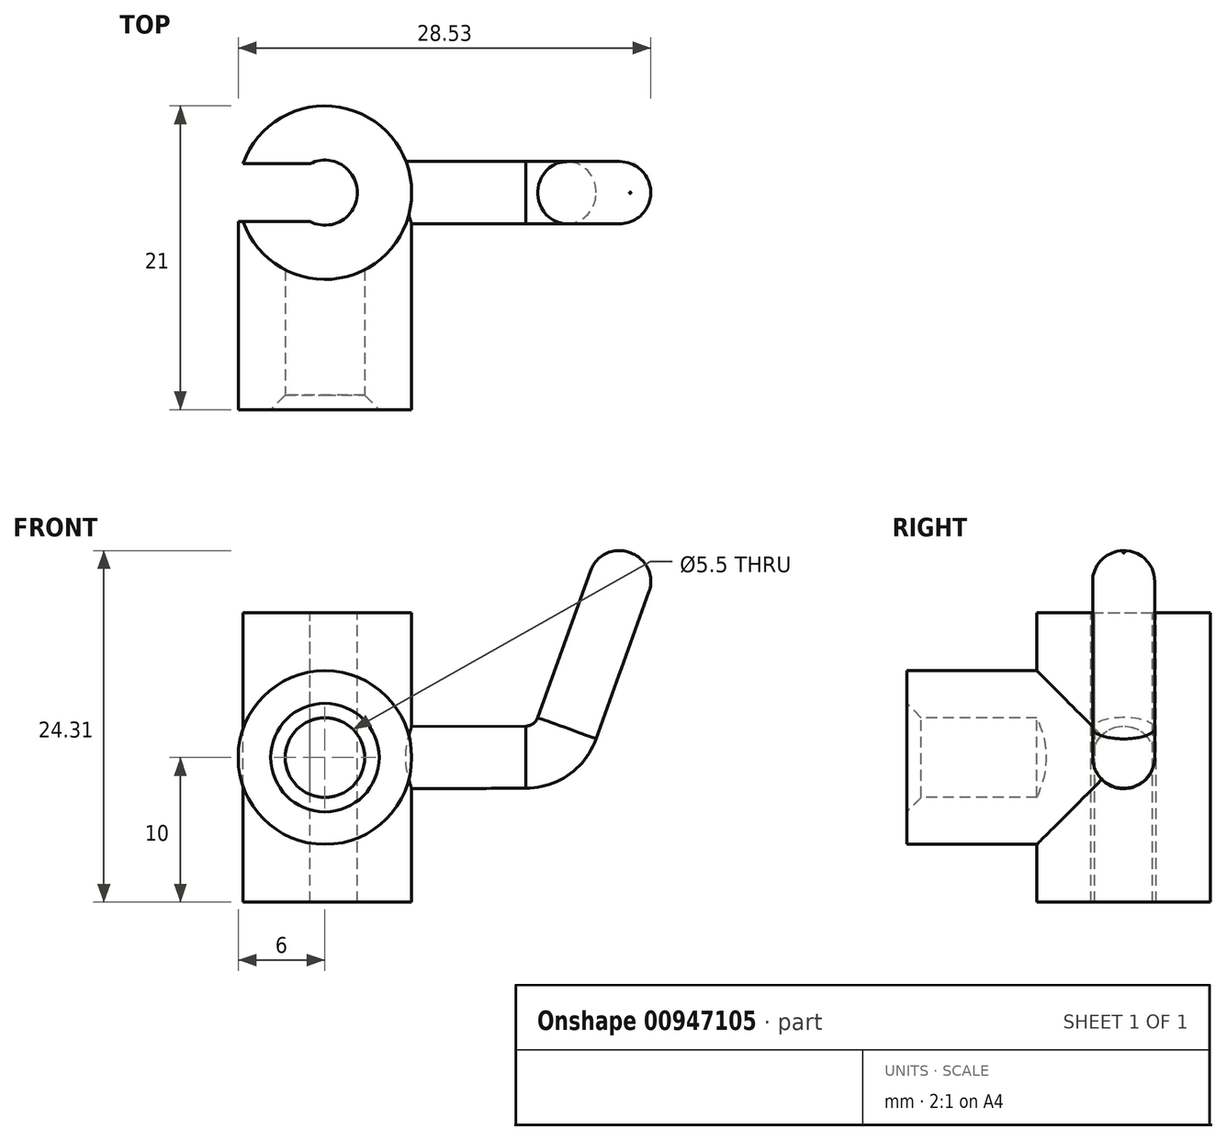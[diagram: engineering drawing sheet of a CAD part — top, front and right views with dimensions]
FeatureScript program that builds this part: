
annotation { "Feature Type Name" : "Feature", "Feature Type Description" : "" }
export const myFeature = defineFeature(function(context is Context, id is Id, definition is map)
    precondition{}
    {
        {
            var Q0;
            Q0=qCreatedBy(makeId("Top.planeOp"),FACE);
            var sketch = newSketch(context, id + "F0", { "sketchPlane" : qUnion([Q0])});
            skCircle(sketch, "E0", {"center": v(0, 0) * mm, "radius": 6 * mm});
            skSolve(sketch);
        }
        {
            var Q0;
            Q0=makeQuery(id+"F0.imprint","IMPRINT",FACE,{"disambiguationData":[TD([[makeQuery(id+"F0.imprint","IMPRINT",EDGE,{"derivedFrom":sQuery(id+"F0.wireOp",EDGE,"E0")}),1.0]])]});
            extrude(context, id + "F1", {"entities" : qUnion([Q0]), "oppositeDirection" : true, "depth" : 20 * mm, "offsetDistance" : 25 * mm});
        }
        {
            var Q0;
            Q0=makeQuery(id+"F1.opExtrude","CAP_FACE",FACE,{"disambiguationData":[OSD([sQuery(id+"F0.wireOp",EDGE,"E0")])],"isStart":true});
            var sketch = newSketch(context, id + "F2", { "sketchPlane" : qUnion([Q0])});
            skCircle(sketch, "E1", {"center": v(0, 0) * mm, "radius": 2.25 * mm});
            skSolve(sketch);
        }
        {
            var Q0;
            Q0=qCreatedBy(makeId("Front.planeOp"),FACE);
            cPlane(context, id + "F3", {"entities" : qUnion([Q0]), "cplaneType" : CPlaneType.OFFSET, "offset" : 15 * mm, "width" : 150 * mm, "height" : 150 * mm});
        }
        {
            var Q0;
            Q0=qCreatedBy(id+"F3.planeOp",FACE);
            var sketch = newSketch(context, id + "F4", { "sketchPlane" : qUnion([Q0])});
            skCircle(sketch, "E2", {"center": v(0, -10) * mm, "radius": 6 * mm});
            skCircle(sketch, "E3", {"center": v(0, -10) * mm, "radius": 2.75 * mm});
            skSolve(sketch);
        }
        {
            var Q0;
            Q0=makeQuery(id+"F4.imprint","IMPRINT",FACE,{"disambiguationData":[TD([[makeQuery(id+"F4.imprint","IMPRINT",EDGE,{"derivedFrom":sQuery(id+"F4.wireOp",EDGE,"E2")}),1.0]])]});
            extrude(context, id + "F5", {"entities" : qUnion([Q0]), "operationType" : NewBodyOperationType.ADD, "oppositeDirection" : true, "depth" : 15 * mm, "offsetDistance" : 25 * mm});
        }
        {
            var Q0;
            Q0=makeQuery(id+"F1.opExtrude","CAP_FACE",FACE,{"disambiguationData":[OSD([sQuery(id+"F0.wireOp",EDGE,"E0")])],"isStart":true});
            var sketch = newSketch(context, id + "F6", { "sketchPlane" : qUnion([Q0])});
            skLineSegment(sketch, "E4.bottom", {"start": v(-8.53, 2) * mm, "end": v(0, 2) * mm});
            skLineSegment(sketch, "E4.top", {"start": v(-8.53, -2) * mm, "end": v(0, -2) * mm});
            skLineSegment(sketch, "E4.left", {"start": v(-8.53, 2) * mm, "end": v(-8.53, -2) * mm});
            skPoint(sketch, "E4.middle", {"position": v(0, 0) * mm});
            skLineSegment(sketch, "E5", {"start": v(0, 2) * mm, "end": v(0, -2) * mm});
            skSolve(sketch);
        }
        {
            var Q0;
            {var subQ0=sQuery(id+"F6.wireOp",EDGE,"E4.bottom");var subQ1=makeQuery(id+"F1.opExtrude","CAP_EDGE",EDGE,{"disambiguationData":[OSD([sQuery(id+"F0.wireOp",EDGE,"E0")])],"isStart":true});var subQ2=makeQuery(id+"F6.imprint","INTERSECT",VERTEX,{"derivedFrom":[subQ1,subQ0]});Q0=makeQuery(id+"F6.imprint","IMPRINT",FACE,{"disambiguationData":[TD([[makeQuery(id+"F6.imprint","IMPRINT",EDGE,{"disambiguationData":[TD([[subQ2,-1.0]])],"derivedFrom":subQ0}),-1.0]])]});}
            var Q1;
            {var subQ0=sQuery(id+"F6.wireOp",EDGE,"E5");Q1=makeQuery(id+"F6.imprint","IMPRINT",FACE,{"disambiguationData":[TD([[makeQuery(id+"F6.imprint","IMPRINT",EDGE,{"derivedFrom":subQ0}),-1.0]])]});}
            var Q2;
            {var subQ0=sQuery(id+"F6.wireOp",EDGE,"E4.left");Q2=makeQuery(id+"F6.imprint","IMPRINT",FACE,{"disambiguationData":[TD([[makeQuery(id+"F6.imprint","IMPRINT",EDGE,{"derivedFrom":subQ0}),1.0]])]});}
            extrude(context, id + "F7", {"entities" : qUnion([Q0, Q1, Q2]), "operationType" : NewBodyOperationType.REMOVE, "endBound" : BoundingType.UP_TO_NEXT, "oppositeDirection" : true, "depth" : 25 * mm, "offsetDistance" : 25 * mm});
        }
        {
            var Q0;
            Q0=makeQuery(id+"F5.opExtrude","CAP_EDGE",EDGE,{"disambiguationData":[OSD([sQuery(id+"F4.wireOp",EDGE,"E3")])],"isStart":true});
            chamfer(context, id + "F8", {"entities" : qUnion([Q0]), "width" : 1 * mm, "tangentPropagation" : true});
        }
        {
            var Q0;
            Q0=qCreatedBy(makeId("Right.planeOp"),FACE);
            cPlane(context, id + "F9", {"entities" : qUnion([Q0]), "cplaneType" : CPlaneType.OFFSET, "offset" : 6 * mm, "width" : 150 * mm, "height" : 150 * mm});
        }
        {
            var Q0;
            Q0=qCreatedBy(makeId("Front.planeOp"),FACE);
            var sketch = newSketch(context, id + "F10", { "sketchPlane" : qUnion([Q0])});
            skLineSegment(sketch, "E6", {"start": v(0, -10) * mm, "end": v(13.9, -9.95) * mm});
            skLineSegment(sketch, "E7", {"start": v(16.71, -7.96) * mm, "end": v(21.08, 4.17) * mm});
            skPoint(sketch, "E8.visualSharp", {"position": v(16, -9.94) * mm});
            skArc(sketch, "E8.filletArc", {"start": v(13.9, -9.95) * mm, "mid": v(15.62, -9.4) * mm, "end": v(16.71, -7.96) * mm});
            skSolve(sketch);
        }
        {
            var Q0;
            Q0=qCreatedBy(id+"F9.planeOp",FACE);
            var sketch = newSketch(context, id + "F11", { "sketchPlane" : qUnion([Q0])});
            skCircle(sketch, "E9", {"center": v(0, -10) * mm, "radius": 2.15 * mm});
            skSolve(sketch);
        }
        {
            var Q0;
            Q0=makeQuery(id+"F11.imprint","IMPRINT",FACE,{"disambiguationData":[TD([[makeQuery(id+"F11.imprint","IMPRINT",EDGE,{"derivedFrom":sQuery(id+"F11.wireOp",EDGE,"E9")}),1.0]])]});
            var Q1;
            Q1=sQuery(id+"F10.wireOp",EDGE,"E6");
            var Q2;
            Q2=sQuery(id+"F10.wireOp",EDGE,"E8.filletArc");
            var Q3;
            Q3=sQuery(id+"F10.wireOp",EDGE,"E7");
            sweep(context, id + "F12", {"operationType" : NewBodyOperationType.ADD, "profiles" : qUnion([Q0]), "path" : qUnion([Q1, Q2, Q3])});
        }
        {
            var Q0;
            Q0=makeQuery(id+"F2.imprint","IMPRINT",FACE,{"disambiguationData":[TD([[makeQuery(id+"F2.imprint","IMPRINT",EDGE,{"derivedFrom":sQuery(id+"F2.wireOp",EDGE,"E1")}),1.0]])]});
            extrude(context, id + "F13", {"entities" : qUnion([Q0]), "operationType" : NewBodyOperationType.REMOVE, "endBound" : BoundingType.THROUGH_ALL, "oppositeDirection" : true, "depth" : 25 * mm, "offsetDistance" : 25 * mm});
        }
        {
            var Q0;
            Q0=makeQuery(id+"F12.opSweep","CAP_EDGE",EDGE,{"disambiguationData":[OSD([sQuery(id+"F10.wireOp",VERTEX,"E7.end"),sQuery(id+"F11.wireOp",EDGE,"E9")])],"isStart":false});
            fillet(context, id + "F14", {"entities" : qUnion([Q0]), "radius" : 2.1 * mm, "tangentPropagation" : true, "allowEdgeOverflow" : false});
        }
    });
